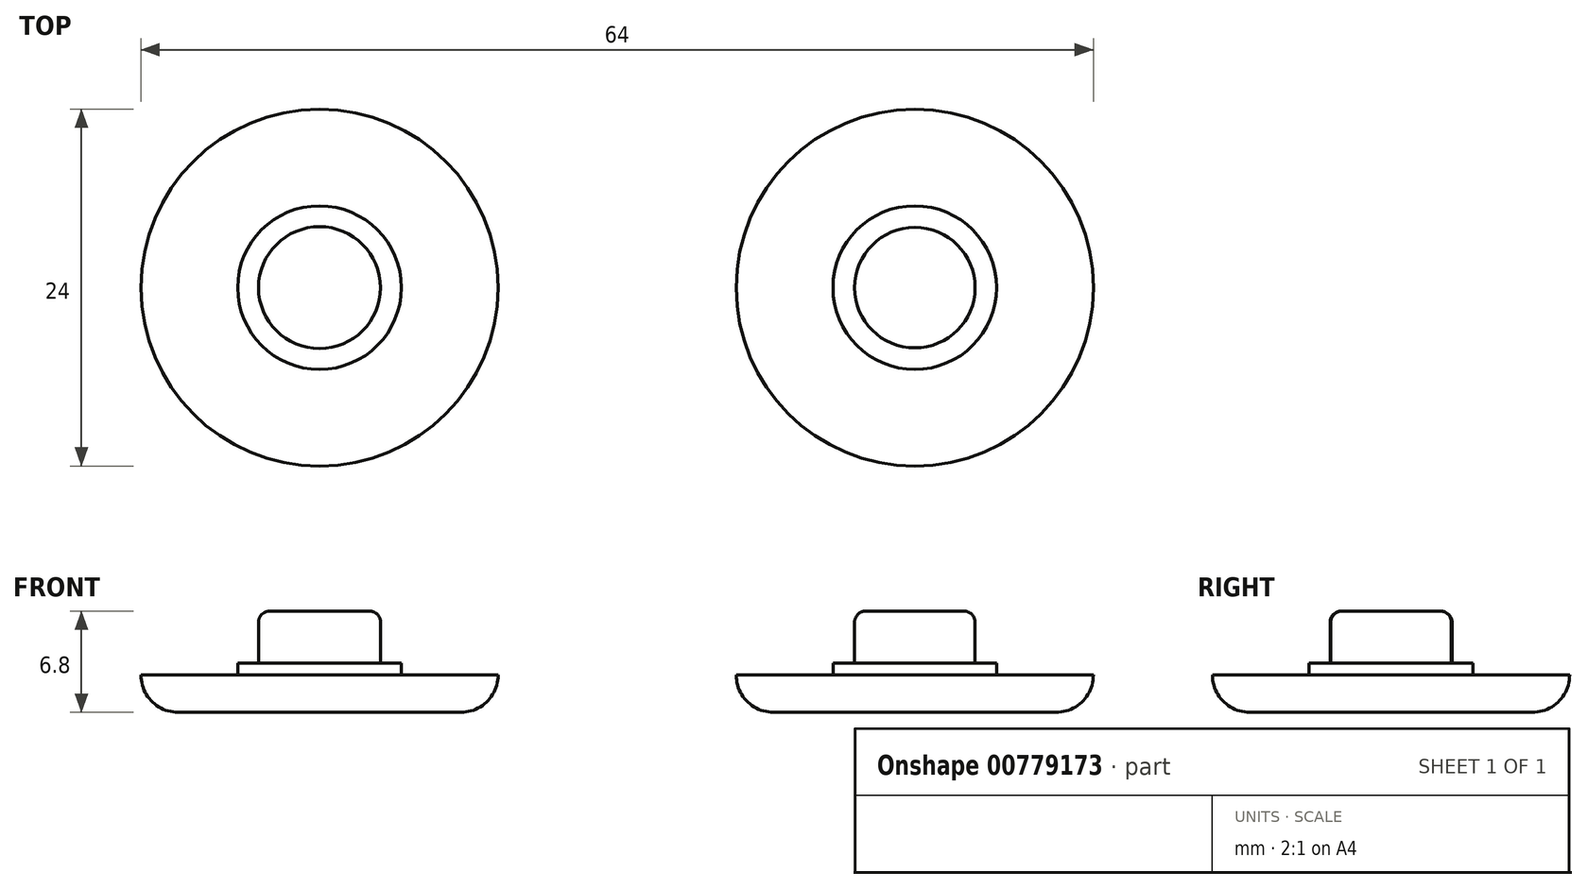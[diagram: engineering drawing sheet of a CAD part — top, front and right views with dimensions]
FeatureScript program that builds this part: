
annotation { "Feature Type Name" : "Feature", "Feature Type Description" : "" }
export const myFeature = defineFeature(function(context is Context, id is Id, definition is map)
    precondition{}
    {
        {
            var Q0;
            Q0=qCreatedBy(makeId("Top.planeOp"),FACE);
            var sketch = newSketch(context, id + "F0", { "sketchPlane" : qUnion([Q0])});
            skCircle(sketch, "E0", {"center": v(0, 0) * mm, "radius": 12 * mm});
            skCircle(sketch, "E1.1.0.0", {"center": v(40, 0) * mm, "radius": 12 * mm});
            skLineSegment(sketch, "E1.direction1", {"start": v(0, 0) * mm, "end": v(40, 0) * mm, "construction": true});
            skSolve(sketch);
        }
        {
            var Q0;
            Q0=qSketchRegion(id+"F0",true);
            extrude(context, id + "F1", {"entities" : qUnion([Q0]), "depth" : 2.5 * mm, "offsetDistance" : 25 * mm});
        }
        {
            var Q0;
            Q0=makeQuery(id+"F1.opExtrude","CAP_FACE",FACE,{"disambiguationData":[OSD([sQuery(id+"F0.wireOp",EDGE,"E0")])],"isStart":false});
            var sketch = newSketch(context, id + "F2", { "sketchPlane" : qUnion([Q0])});
            skCircle(sketch, "E2", {"center": v(0, 0) * mm, "radius": 5.5 * mm});
            skCircle(sketch, "E3", {"center": v(40, 0) * mm, "radius": 5.5 * mm});
            skSolve(sketch);
        }
        {
            var Q0;
            Q0=qSketchRegion(id+"F2",true);
            extrude(context, id + "F3", {"entities" : qUnion([Q0]), "operationType" : NewBodyOperationType.ADD, "depth" : .8 * mm, "offsetDistance" : 25 * mm});
        }
        {
            var Q0;
            Q0=makeQuery(id+"F3.opExtrude","CAP_FACE",FACE,{"disambiguationData":[OSD([sQuery(id+"F2.wireOp",EDGE,"E2")])],"isStart":false});
            var sketch = newSketch(context, id + "F4", { "sketchPlane" : qUnion([Q0])});
            skCircle(sketch, "E4", {"center": v(0, 0) * mm, "radius": 4.1 * mm});
            skCircle(sketch, "E5", {"center": v(40, 0) * mm, "radius": 4.05 * mm});
            skSolve(sketch);
        }
        {
            var Q0;
            Q0=qSketchRegion(id+"F4",true);
            extrude(context, id + "F5", {"entities" : qUnion([Q0]), "operationType" : NewBodyOperationType.ADD, "depth" : 3.5 * mm, "offsetDistance" : 25 * mm});
        }
        {
            var Q0;
            Q0=makeQuery(id+"F1.opExtrude","CAP_EDGE",EDGE,{"disambiguationData":[OSD([sQuery(id+"F0.wireOp",EDGE,"E0")])],"isStart":true});
            var Q1;
            Q1=makeQuery(id+"F1.opExtrude","CAP_EDGE",EDGE,{"disambiguationData":[OSD([sQuery(id+"F0.wireOp",EDGE,"E1.1.0.0")])],"isStart":true});
            fillet(context, id + "F6", {"entities" : qUnion([Q0, Q1]), "radius" : 2.5 * mm, "tangentPropagation" : true, "allowEdgeOverflow" : false});
        }
        {
            var Q0;
            Q0=makeQuery(id+"F5.opExtrude","CAP_EDGE",EDGE,{"disambiguationData":[OSD([sQuery(id+"F4.wireOp",EDGE,"E4")])],"isStart":false});
            var Q1;
            Q1=makeQuery(id+"F5.opExtrude","CAP_EDGE",EDGE,{"disambiguationData":[OSD([sQuery(id+"F4.wireOp",EDGE,"E5")])],"isStart":false});
            fillet(context, id + "F7", {"entities" : qUnion([Q0, Q1]), "radius" : .75 * mm, "tangentPropagation" : true, "allowEdgeOverflow" : false});
        }
    });
